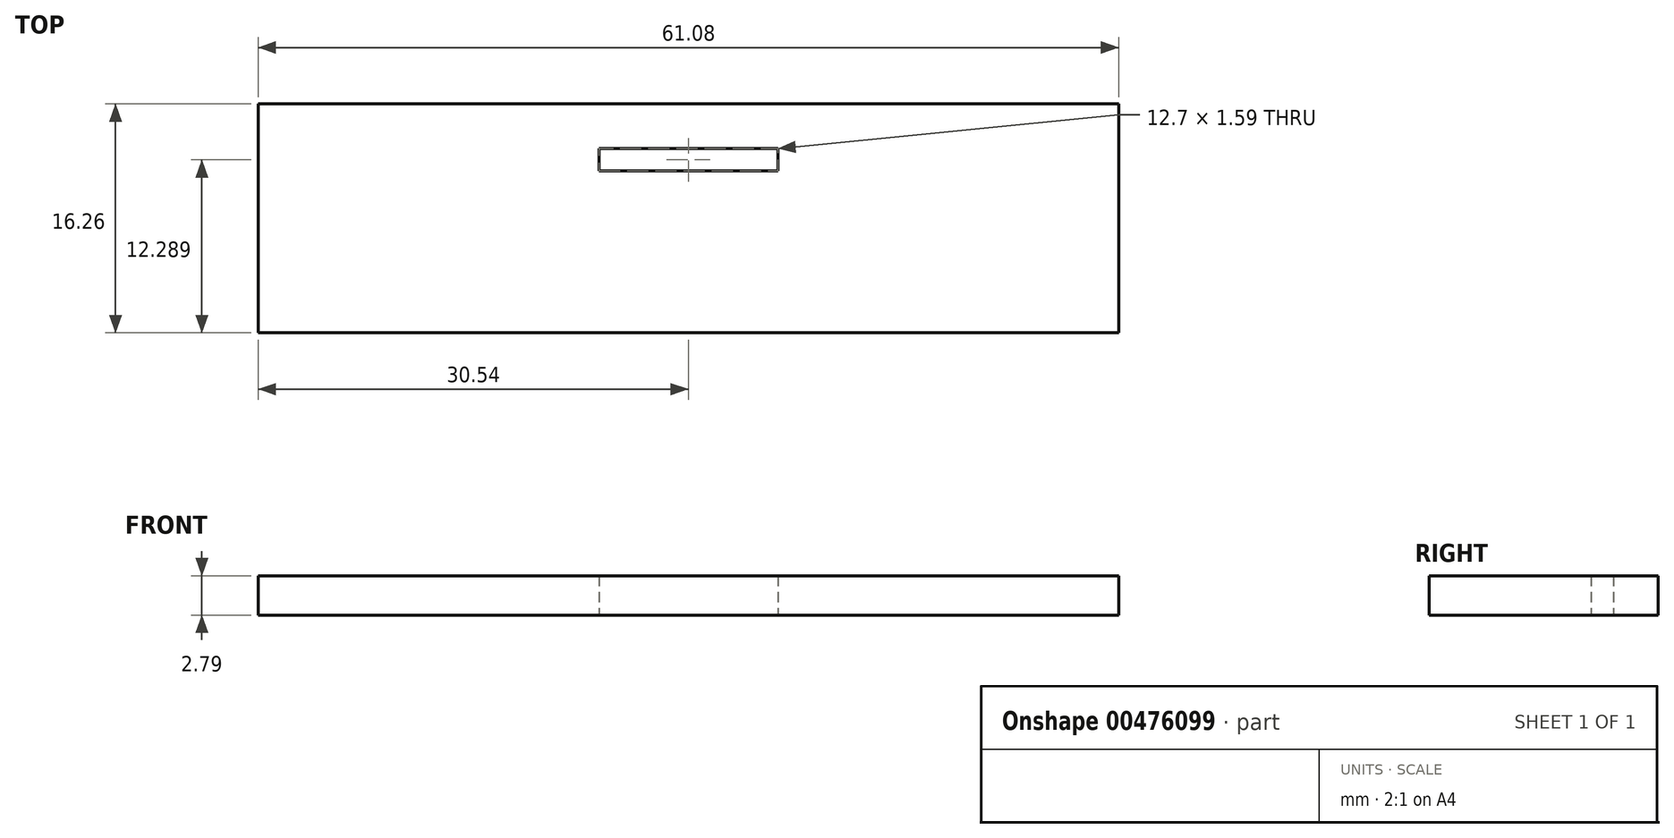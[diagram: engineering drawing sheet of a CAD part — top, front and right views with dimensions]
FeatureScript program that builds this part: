
annotation { "Feature Type Name" : "Feature", "Feature Type Description" : "" }
export const myFeature = defineFeature(function(context is Context, id is Id, definition is map)
    precondition{}
    {
        {
            var Q0;
            Q0=qCreatedBy(makeId("Top.planeOp"),FACE);
            var sketch = newSketch(context, id + "F0", { "sketchPlane" : qUnion([Q0])});
            skLineSegment(sketch, "E0.bottom", {"start": v(30.54, -8.13) * mm, "end": v(-30.54, -8.13) * mm});
            skLineSegment(sketch, "E0.top", {"start": v(30.54, 8.13) * mm, "end": v(-30.54, 8.13) * mm});
            skLineSegment(sketch, "E0.left", {"start": v(30.54, -8.13) * mm, "end": v(30.54, 8.13) * mm});
            skLineSegment(sketch, "E0.right", {"start": v(-30.54, -8.13) * mm, "end": v(-30.54, 8.13) * mm});
            skPoint(sketch, "E0.middle", {"position": v(0, 0) * mm});
            skSolve(sketch);
        }
        {
            var Q0;
            Q0=makeQuery(id+"F0.imprint","IMPRINT",FACE,{"disambiguationData":[TD([[makeQuery(id+"F0.imprint","IMPRINT",EDGE,{"derivedFrom":sQuery(id+"F0.wireOp",EDGE,"E0.bottom")}),-1.0]])]});
            extrude(context, id + "F1", {"entities" : qUnion([Q0]), "depth" : 2.8 * mm, "offsetDistance" : 25.4 * mm});
        }
        {
            var Q0;
            Q0=makeQuery(id+"F1.opExtrude","CAP_FACE",FACE,{"disambiguationData":[OSD([sQuery(id+"F0.wireOp",EDGE,"E0.bottom"),sQuery(id+"F0.wireOp",EDGE,"E0.top"),sQuery(id+"F0.wireOp",EDGE,"E0.left"),sQuery(id+"F0.wireOp",EDGE,"E0.right")])],"isStart":true});
            var sketch = newSketch(context, id + "F2", { "sketchPlane" : qUnion([Q0])});
            skLineSegment(sketch, "E1.bottom", {"start": v(-6.35, -3.37) * mm, "end": v(6.35, -3.37) * mm});
            skLineSegment(sketch, "E1.top", {"start": v(-6.35, -4.95) * mm, "end": v(6.35, -4.95) * mm});
            skLineSegment(sketch, "E1.left", {"start": v(-6.35, -3.37) * mm, "end": v(-6.35, -4.95) * mm});
            skLineSegment(sketch, "E1.right", {"start": v(6.35, -3.37) * mm, "end": v(6.35, -4.95) * mm});
            skPoint(sketch, "E1.middle", {"position": v(0, -4.16) * mm});
            skSolve(sketch);
        }
        {
            var Q0;
            Q0 = qSketchRegion(id + "F2", true);
            var Q1;
            Q1=makeQuery(id+"F1.opExtrude","CAP_FACE",FACE,{"disambiguationData":[OSD([sQuery(id+"F0.wireOp",EDGE,"E0.bottom"),sQuery(id+"F0.wireOp",EDGE,"E0.top"),sQuery(id+"F0.wireOp",EDGE,"E0.left"),sQuery(id+"F0.wireOp",EDGE,"E0.right")])],"isStart":false});
            extrude(context, id + "F3", {"entities" : qUnion([Q0]), "operationType" : NewBodyOperationType.REMOVE, "endBound" : BoundingType.UP_TO_SURFACE, "oppositeDirection" : true, "depth" : 25.4 * mm, "endBoundEntityFace" : qUnion([Q1]), "offsetDistance" : 25.4 * mm});
        }
    });
